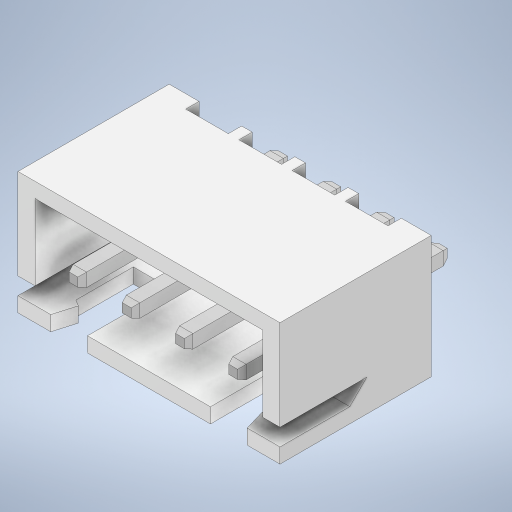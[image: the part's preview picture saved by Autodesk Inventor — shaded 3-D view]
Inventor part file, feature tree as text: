
AUTODESK INVENTOR PART (.ipt)
format: ipt  version: 2023 (Build 270158000, 158)  size: 486,400 bytes
history: native  units: mm
features: extrude x2, sketch x2, imported_body x1
ambient origin geometry x8: Origin, YZ Plane, XZ Plane, XY Plane, X Axis, Y Axis, Z Axis, Center Point
bodies: Solid1 (feature_tree)
feature tree (5):
  extrude  "Extrusion1"  TaperAngle=0.0deg  [1 undecoded]
  extrude  "Extrusion2"  TaperAngle=0.0deg  [1 undecoded]
  sketch  "Sketch1"  dims[d0=12.5mm d1=0.0mm]
  sketch  "Sketch2"  dims[d2=-0.103mm d3=0.0mm d4=0.0mm d5=17.5mm d6=5.0mm d7=0.0mm d8=0.0mm]
  imported_body  "Base1"
note: 2 required parameter values undecoded (feature->parameter linkage not recoverable at this tier; creation-order binding heuristic only, values carry confidence <= 0.55)
